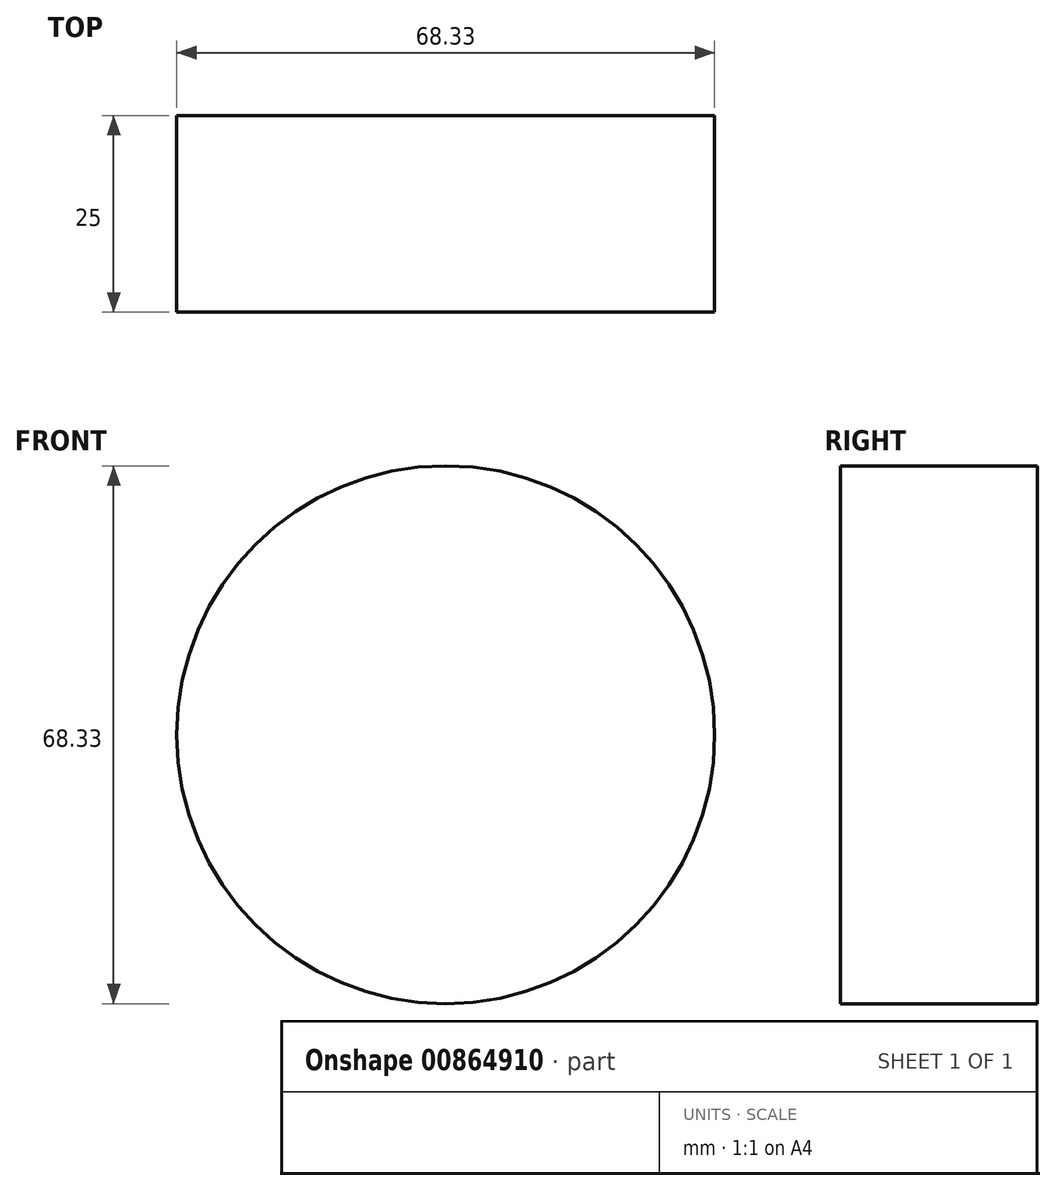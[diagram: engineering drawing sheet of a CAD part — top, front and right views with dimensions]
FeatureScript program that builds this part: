
annotation { "Feature Type Name" : "Feature", "Feature Type Description" : "" }
export const myFeature = defineFeature(function(context is Context, id is Id, definition is map)
    precondition{}
    {
        {
            var Q0;
            Q0=qCreatedBy(makeId("Front.planeOp"),FACE);
            var sketch = newSketch(context, id + "F0", { "sketchPlane" : qUnion([Q0])});
            skCircle(sketch, "E0", {"center": v(-124.55, -30.74) * mm, "radius": 34.16 * mm});
            skSolve(sketch);
        }
        {
            var Q0;
            Q0 = qSketchRegion(id + "F0", true);
            extrude(context, id + "F1", {"entities" : qUnion([Q0]), "depth" : 25 * mm, "offsetDistance" : 25 * mm});
        }
    });
